# Revit family: CADS_AIRFLOWdev_Fan_iCON15
name_source: partatom
category: Mechanical Equipment
revit_build: Autodesk Revit 2015 (Build: 20160512_1515(x64)
units: mm (PartAtom-declared; Revit-internal decimal feet)

## types (1)
- iC15
    2SFT = iCON15_Modules : 2 Speed Humidity Pull Cord Boost
    6MonthlyMaintenance = Visually inspect system, clean the fan and ducting if necessary
    A = 197 mm
    AccessClearanceBottom = 350 mm
    AccessClearanceFront = 350 mm
    AccessClearanceLeft = 350 mm
    AccessClearanceRear = 0 mm  [stored 0 ft]
    AccessClearanceRight = 350 mm
    AccessClearanceTop = 350 mm
    AnthraciteFT = CADS_AIRFLOWdev_Fan_iCON15_Covers : Anthracite
    AssemblyPlace = UKNOWN
    AssetType = Fixed
    BMSLinks = No
    Body = CADS_AirFlow_White
    C = 68 mm
    CADS_Index = 0
    CEApproval = Yes
    CVFT = iCON15_Modules : Continuous Ventilation
    Category = Pr_65_67_29_05:Axial Flow Fans
    ChromeFT = CADS_AIRFLOWdev_Fan_iCON15_Covers : Chrome
    Color = White
(optional Anthracite (52634503), Sandstone (52634505), Chrome (52634502) and Silver (52634504) covers are available)
    Controls = Basic on/off functionality controlled by external switch
The following additional, interchangeable modules can be fitted to the iCON15:
Pull cord (72573602)
Timer (72612601)
Humidity, Pull cord with Timer (72687103)
Motion sensor with timer overrun (72687104)
Motion sensor humidity timer (72687102)
Continuous Ventilation at 8/13 l/sec (72675701)
Delayed Timer with Pull cord (72675702)
2 Speed Humidity Pull Cord Boost (72675703)
    D = 100 mm  [stored 0.328084 ft]
    DTFT = iCON15_Modules : Delayed Timer With Pull Cord
    Default Elevation = 1219 mm
    Description = An intermittent extract fan with interchangeable modular controls and covers and a Red Dot Design Award winner
    DesignOfDomesticVentilation = This fan should provide the minimum flow rates outlined and installed in line with Approved Document Part F of the Building Regulations.
    Ductwork = 100mm flexible or rigid
    DurationUnit = Year
    E = 40 mm  [stored 0.131234 ft]
    ErPEnergyRating = C
    ErPFiche = https://www.airflow.com
    Exclusions = Hasn't been installed or used in accordance with the instructions
Connected with an unsuitable electrical supply
Has been misused, neglected or damaged
Modified or repaired by someone not authorised by Airflow Developments Ltd
Hasn't been installed according to Building Regulations or IEEE wiring regulations
    ExpectedServiceLife = 3
    ExternalExhaustAirTerminals = 90% free air grille
    Fan = Domestic intermittent axial fan
    Features = Up to 19l/sec
Stylish design, with unique iris shutter
Interchangeable modular control
IPX4 rated
Sound Levels from only 30.3dB(A)
Red Dot Design Award Winner
    Finish = Matte
    FireControlPanelLinks = No
    GlobalTradeItemNumber = 5019009307633
    Grade = Virgin
    GrossWeight = 0.74 kg
    HPCFT = iCON15_Modules : Humidity Pull Cord With Timer Overrun
    HasPartWinding = Yes
    HasProtectiveEarth = No
    IP_Code = IPX4
    ISO140001 = Yes
    ISO90001 = Yes
    IfcExportAs = IfcFanType
    IfcExportType = NOTDEFINED
    InsulationStandardClass = Double Insulated
    IsExtendedWarranty = No
    IsGuarded = Yes
    MSHFT = iCON15_Modules : Motion Sensor Humidity Timer
    MSTFT = iCON15_Modules : Motion Sensor With Timer Overrun
    Manufacturer = Airflow Developments Ltd
    ManufacturerAddress = Aidelle House
Lancaster Road
Cressex Business Park
High Wycombe
Bucks
HP123QP
    ManufacturerTelephone = 01494 525252
    ManufacturerWebsite = www.airflow.com
    Material = Plastic
    ModelLabel = iCON 15
    ModelReference = 72683501
    MotorDriveType = Direct Drive
    MotorEnclosureType = Totally Enclosed Air Over
    NBSCode = 90-45-30/310 Axial flow fans;
    NominalAirFlowRate = 19.0 L/s
    NominalFrequencyRange = 50-60
    NominalHeight = 197 mm
    NominalLength = 109 mm
    NominalPowerRate = 9 W
    NominalRotationSpeed = 40 Hz
    NominalStaticPressure = 30.0 Pa
    NominalWidth = 197 mm
    NumberOfPoles = 1
    OperationAndMaintenanceManual = https://www.airflow.com
    OperationAndMaintenanceManualAccessories = https://www.airflow.com
    OperationTemperatureRange = up to 40°C
    PCFT = iCON15_Modules : Pull Cord
    PointOfContact = Airflow Developments Ltd
    PowerSource = System-powered
    PressureCurve = https://www.airflow.com
    ProductLiterature = https://www.airflow.com
    ProductLiteratureAccessories = https://www.airflow.com
    ProductionYear = 2017
    Quantity = 1
    QuietMarkApproval = No
    RatedCurrent = 3 A
    RatedVoltage = 230 V
    RedDotDesignAward = Yes
    ReplacementCost = 74.064
    RoomExtractAirTerminalDevices = En-suite, toilet and bathroom fan
    SandstoneFT = CADS_AIRFLOWdev_Fan_iCON15_Covers : Standstone
    ServiceLifeDuration = 3
    ServiceLifeType = ExpectedServiceLife
    Shape = Round
    ShippingWeight = 1.05 kg
    SilverFT = CADS_AIRFLOWdev_Fan_iCON15_Covers : Silver
    Size = 108.5 x 197 x 197
    StartingTime = 5.0 s
    Status = New
    SupplyPhase = 1
    TFT = iCON15_Modules : Timer
    Type = iC15
    Uniclass2015 = Pr_65_67_29_05
    WarrantyContent = Covered against faulty material or workmanship - not reinstallation if needed
    WarrantyGuarantor = Airflow Developments Ltd
    WarrantyPeriod = 2
    WarrantyPeriodForMotors = 1
    WarrantyPeriodWhenRegistered = 3

note: [stored X ft] marks values corroborated as IEEE doubles in the binary element streams (Revit-internal decimal feet)

## geometry (parser evidence)
native form markers: Blend x6, Sweep x9
no freeform markers — native parametric forms only
